# Revit family: P560262-169
name_source: partatom
category: Lighting Fixtures
units: mm (PartAtom-declared; Revit-internal decimal feet)

## family parameters
Cut with Voids When Loaded = No
Host = Face
Light Source = Yes
OmniClass Number = 23.80.70.11.14.17
OmniClass Title = Direct/Indirect
Part Type = Normal
Room Calculation Point = No
Round Connector Dimension = Use Diameter
Shared = Yes

## types (1)
- P560262-169
    Apparent Load = 60 VA
    Assembly Code = D5020200
    Color Filter = 16777215
    Connector Description = Lighting Connector
    Default Elevation = 48 "
    Description = Wakeford Collection One-Light Antique Copper and Clear Water Glass Transitional Style Medium Outdoor Wall Lantern
    Dimming Lamp Color Temperature Shift = <None>
    Features = Integrate a nostalgic look with modern sophistication with the Wakeford Collection 1-Light Antique Copper Clear Water Transitional Outdoor Medium Wall Lantern Light. A cross-brace design with elements of crown molding trim all coated in an antique copper finish gives the lantern a nostalgic look. A light source glows through textured water glass panes for vintage aesthetic.
Application: Integrated a nostalgic look with modern sophistication with the Wakeford Collection 1-Light Antique Copper Clear Water Transitional Outdoor Medium Wall Lantern Light ideal for any porch, patio, deck, entryway, bedroom, foyer, barn, or garage.
Styles: Perfect for transitional and traditional style settings.
Finish: A cross-brace design with elements of crown molding trim all coated in an antique copper finish gives the lantern a nostalgic look.
Materials: Constructed from steel to ensure a long product lifespan.
Glass/Shades: A light source glows through textured water glass panes for vintage aesthetic.
Bulbs: For ideal illumination, use 1 medium base bulb that is sold separately (60w max - LED/CFL/incandescent). Compatible with dimmable bulbs.
Dimensions: Measures 10-inch width by 21-1/2-inch height.
Certifications: cCSAus wet location listed.
Pairs With: Pairs with the Barlowe collection from Progress Lighting.
Warranty: Our 1-Year Limited Warranty guarantees your complete satisfaction with your purchase and includes professional after-sales customer service support.
    Fixture distribution = Direct
    Glass = Paint - Hubbell - White Texture
    Housing Material = Hubbell - Metal - Copper
    Lamp = LED
    Length = 21.5 "
    Load Classification = Lighting
    Manufacturer = Progress Lighting
    Model = P560262-169
    Photometric Web File = generic.ies
    Power Factor = 1
    Product Documentation Link = https://hubbellcdn.com
    Product Link = https://www.hubbell.com
    Tilt Angle = 180.00°
    URL = https://www.hubbell.com
    Voltage = 120 V
    Warranty = 1 year Warranty
    Wattage Comments = 60W
    Watts = 60 W
    Width = 10 "

## geometry (parser evidence)
native form markers: Sweep x5
no freeform markers — native parametric forms only
